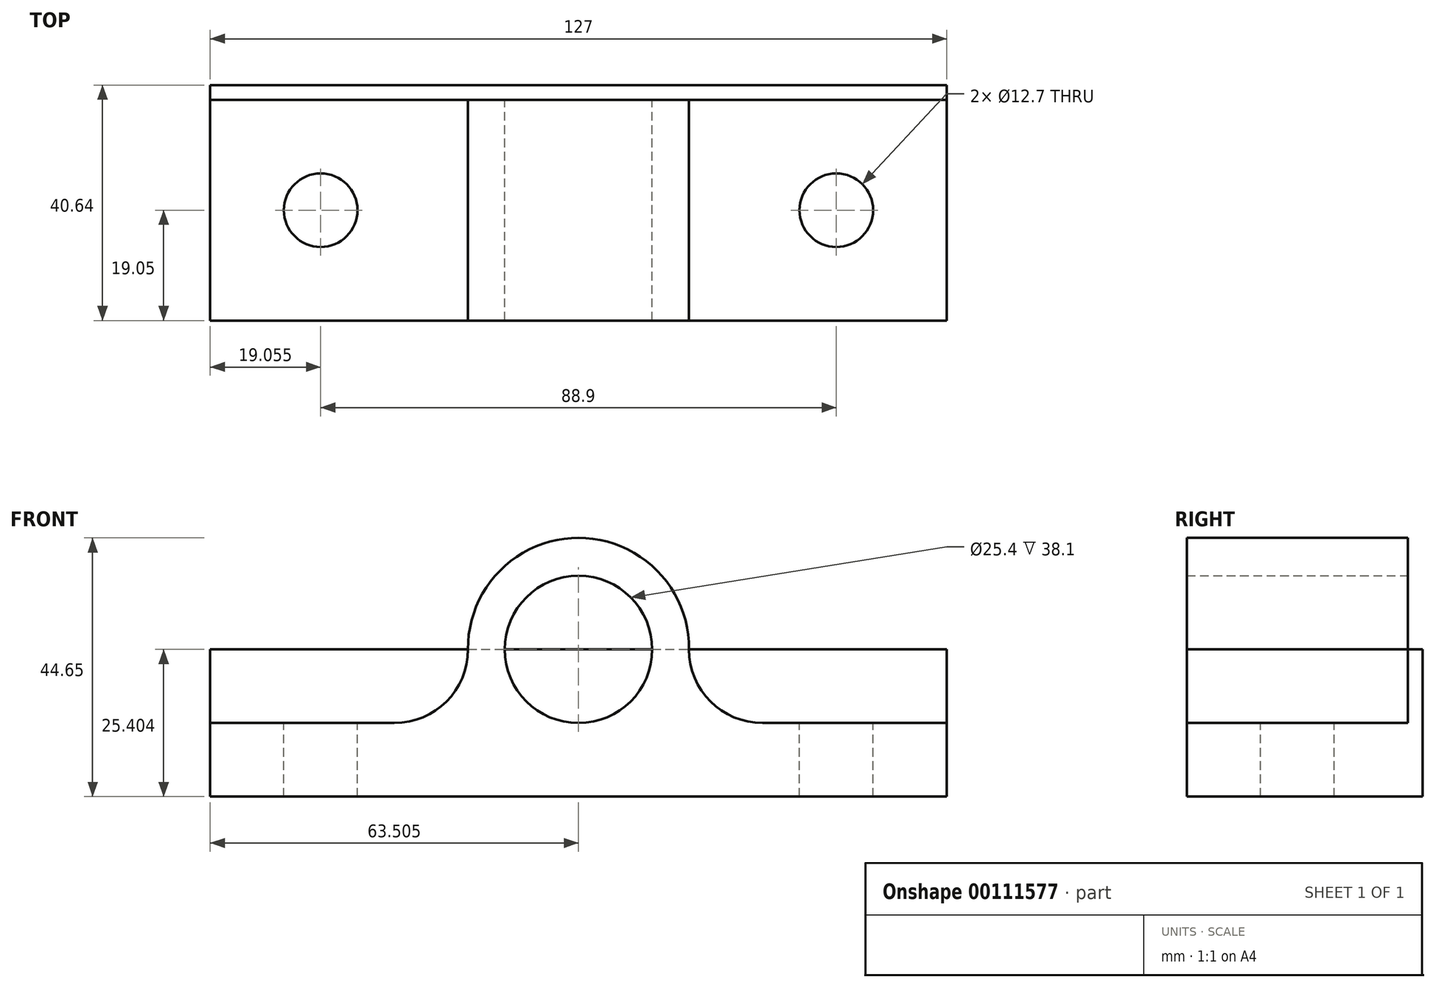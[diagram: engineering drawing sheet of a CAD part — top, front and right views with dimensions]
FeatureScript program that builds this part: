
annotation { "Feature Type Name" : "Feature", "Feature Type Description" : "" }
export const myFeature = defineFeature(function(context is Context, id is Id, definition is map)
    precondition{}
    {
        {
            var Q0;
            Q0=qCreatedBy(makeId("Front.planeOp"),FACE);
            var sketch = newSketch(context, id + "F0", { "sketchPlane" : qUnion([Q0])});
            skLineSegment(sketch, "E0", {"start": v(-66.13, 3.03) * mm, "end": v(-66.13, -22.37) * mm});
            skLineSegment(sketch, "E1", {"start": v(-66.13, -22.37) * mm, "end": v(60.87, -22.37) * mm});
            skLineSegment(sketch, "E2", {"start": v(60.87, 3.03) * mm, "end": v(60.87, -22.37) * mm});
            skLineSegment(sketch, "E3", {"start": v(-66.13, 3.03) * mm, "end": v(60.87, 3.03) * mm});
            skSolve(sketch);
        }
        {
            var Q0;
            Q0 = qSketchRegion(id + "F0", true);
            var Q1;
            Q1=makeQuery(id+"F0.imprint","IMPRINT",FACE,{"disambiguationData":[TD([[makeQuery(id+"F0.imprint","IMPRINT",EDGE,{"derivedFrom":sQuery(id+"F0.wireOp",EDGE,"E0")}),1.0]])]});
            extrude(context, id + "F1", {"entities" : qUnion([Q0, Q1]), "depth" : 2.54 * mm});
        }
        {
            var Q0;
            Q0=makeQuery(id+"F1.opExtrude","CAP_FACE",FACE,{"disambiguationData":[OSD([sQuery(id+"F0.wireOp",EDGE,"E0"),sQuery(id+"F0.wireOp",EDGE,"E1"),sQuery(id+"F0.wireOp",EDGE,"E2"),sQuery(id+"F0.wireOp",EDGE,"E3")])],"isStart":false});
            var sketch = newSketch(context, id + "F2", { "sketchPlane" : qUnion([Q0])});
            skPoint(sketch, "E4.visualSharp", {"position": v(19.13, 3.03) * mm});
            skPoint(sketch, "E5.visualSharp", {"position": v(-31.42, 3.03) * mm});
            skLineSegment(sketch, "E6", {"start": v(-66.13, -9.67) * mm, "end": v(-43.25, -9.67) * mm});
            skLineSegment(sketch, "E7", {"start": v(60.87, -9.67) * mm, "end": v(38, -9.67) * mm});
            skLineSegment(sketch, "E8", {"start": v(-43.25, -9.67) * mm, "end": v(-34.38, -9.67) * mm});
            skLineSegment(sketch, "E9", {"start": v(38, -9.67) * mm, "end": v(29.12, -9.67) * mm});
            skLineSegment(sketch, "E10", {"start": v(-2.63, -22.37) * mm, "end": v(-2.63, 3.03) * mm});
            skCircle(sketch, "E11", {"center": v(-2.63, 3.03) * mm, "radius": 12.7 * mm});
            skPoint(sketch, "E12.visualSharp", {"position": v(-21.68, -9.67) * mm});
            skArc(sketch, "E12.filletArc", {"start": v(-34.38, -9.67) * mm, "mid": v(-25.4, -5.95) * mm, "end": v(-21.68, 3.03) * mm});
            skPoint(sketch, "E13.visualSharp", {"position": v(16.42, -9.67) * mm});
            skArc(sketch, "E13.filletArc", {"start": v(16.42, 3.03) * mm, "mid": v(20.14, -5.95) * mm, "end": v(29.12, -9.67) * mm});
            skArc(sketch, "E14", {"start": v(16.42, 3.03) * mm, "mid": v(-2.63, 22.28) * mm, "end": v(-21.68, 3.03) * mm});
            skSolve(sketch);
        }
        {
            var Q0;
            {var subQ8=sQuery(id+"F2.wireOp",EDGE,"E6");Q0=makeQuery(id+"F2.imprint","IMPRINT",FACE,{"disambiguationData":[TD([[makeQuery(id+"F2.imprint","IMPRINT",EDGE,{"derivedFrom":subQ8}),-1.0]])]});}
            var Q1;
            {var subQ4=sQuery(id+"F2.wireOp",EDGE,"E14");Q1=makeQuery(id+"F2.imprint","IMPRINT",FACE,{"disambiguationData":[TD([[makeQuery(id+"F2.imprint","IMPRINT",EDGE,{"derivedFrom":subQ4}),1.0]])]});}
            var Q2;
            {var subQ8=sQuery(id+"F2.wireOp",EDGE,"E7");Q2=makeQuery(id+"F2.imprint","IMPRINT",FACE,{"disambiguationData":[TD([[makeQuery(id+"F2.imprint","IMPRINT",EDGE,{"derivedFrom":subQ8}),1.0]])]});}
            extrude(context, id + "F3", {"entities" : qUnion([Q0, Q1, Q2]), "operationType" : NewBodyOperationType.ADD, "depth" : 38.1 * mm});
        }
        {
            var Q0;
            Q0=makeQuery(id+"F3.opExtrude","SWEPT_FACE",FACE,{"disambiguationData":[OSD([sQuery(id+"F2.wireOp",EDGE,"E6"),sQuery(id+"F2.wireOp",EDGE,"E8")])]});
            var sketch = newSketch(context, id + "F4", { "sketchPlane" : qUnion([Q0])});
            skCircle(sketch, "E15", {"center": v(-47.08, -21.59) * mm, "radius": 6.35 * mm});
            skCircle(sketch, "E16", {"center": v(41.82, -21.59) * mm, "radius": 6.35 * mm});
            skSolve(sketch);
        }
        {
            var Q0;
            Q0=makeQuery(id+"F4.imprint","IMPRINT",FACE,{"disambiguationData":[TD([[makeQuery(id+"F4.imprint","IMPRINT",EDGE,{"derivedFrom":sQuery(id+"F4.wireOp",EDGE,"E16")}),1.0]])]});
            var Q1;
            Q1=makeQuery(id+"F4.imprint","IMPRINT",FACE,{"disambiguationData":[TD([[makeQuery(id+"F4.imprint","IMPRINT",EDGE,{"derivedFrom":sQuery(id+"F4.wireOp",EDGE,"E15")}),1.0]])]});
            extrude(context, id + "F5", {"entities" : qUnion([Q0, Q1]), "operationType" : NewBodyOperationType.REMOVE, "oppositeDirection" : true, "depth" : 25.4 * mm});
        }
    });
